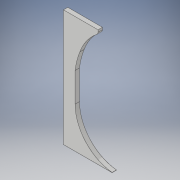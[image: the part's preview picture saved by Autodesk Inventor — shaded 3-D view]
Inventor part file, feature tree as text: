
AUTODESK INVENTOR PART (.ipt)
format: ipt  version: 2018 (Build 220112000, 112)  size: 161,792 bytes
history: native  units: in
note: dims shown in document units (in); Inventor stores cm internally (conversion verified against a paired STEP export)
features: fillet x2, extrude x1, sketch x1
ambient origin geometry x8: Origin, YZ Plane, XZ Plane, XY Plane, X Axis, Y Axis, Z Axis, Center Point
bodies: Body1 (feature_tree)
feature tree (4):
  extrude  "Extrusion2"  Depth=0.0156in
  fillet  "Fillet1"  Radius=12.0in
  fillet  "Fillet4"  Radius=6.5in
  sketch  "Sketch1"  dims[d0=24.0in d1=8.25in d2=12.0in d3=6.5in d4=6.5in d5=12.0in d6=7.0in d7=7.0in d8=1.0in d9=0.5in d10=135.0deg d11=6.5in d12=135.0deg d13=6.5in d14=7.0in d15=0.625in d16=1.0in d17=5.0in d20=5.0in d21=3.0in d22=6.0in d23=1.0in d24=2.0in d25=5.0in d26=0.8727in d33=6.25in d34=0.8727in d35=1.0994in d36=6.25in d37=180.0deg d45=150.0deg d46=6.25in d47=180.0deg d72=26.0in d73=20.0in d74=90.0deg d75=0.75in d76=0.0in d77=5.9332in d78=0.6126in d79=0.5in d82=0.0156in]
